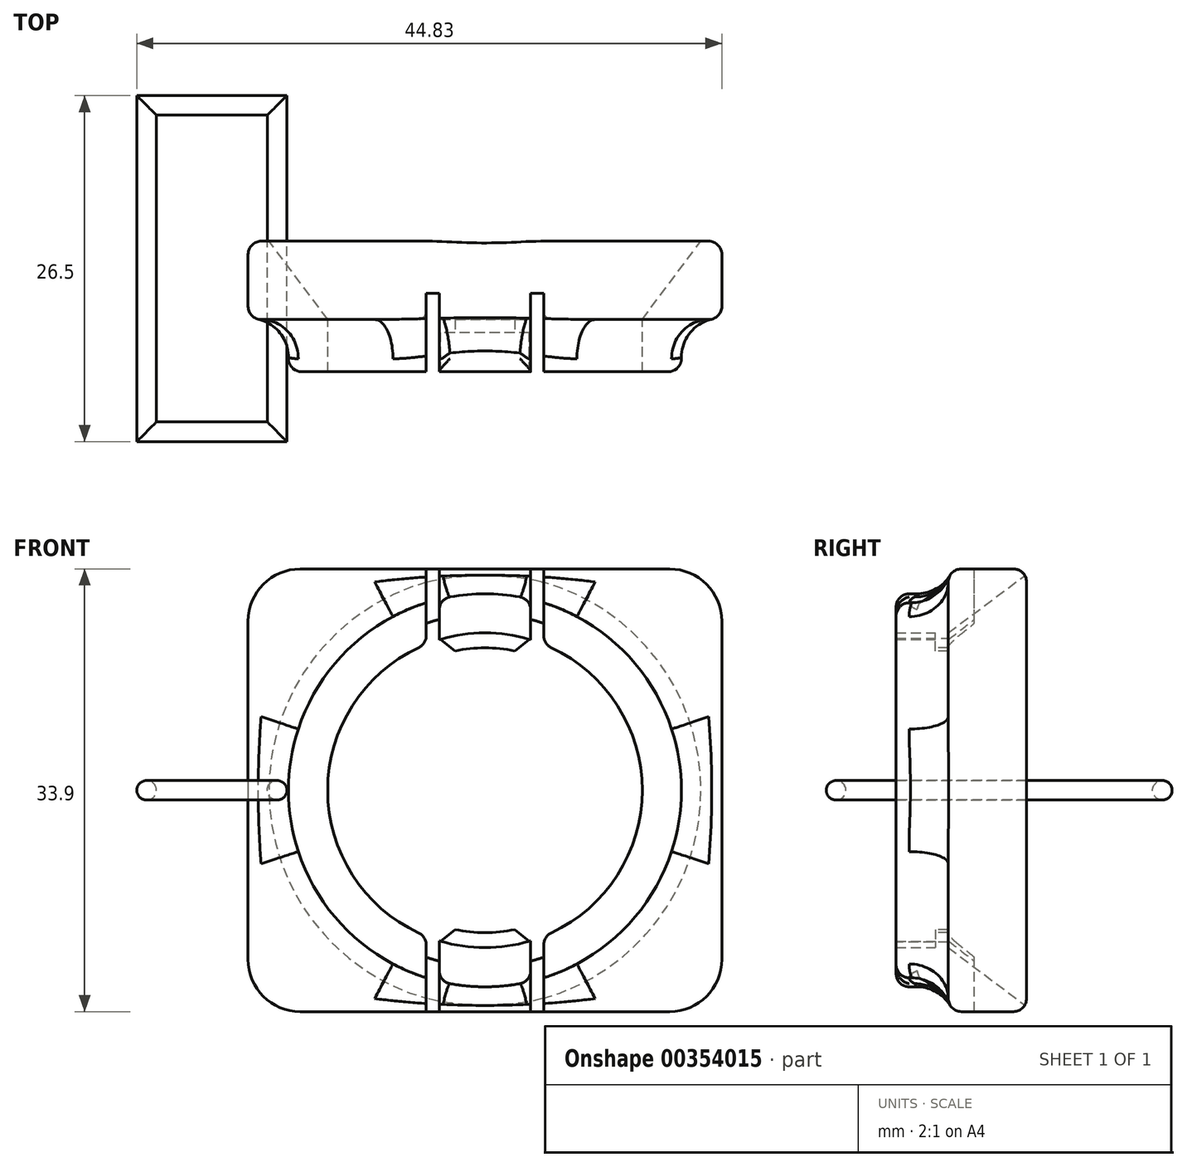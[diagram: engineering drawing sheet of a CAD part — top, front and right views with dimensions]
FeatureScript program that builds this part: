
annotation { "Feature Type Name" : "Feature", "Feature Type Description" : "" }
export const myFeature = defineFeature(function(context is Context, id is Id, definition is map)
    precondition{}
    {
        {
            var Q0;
            Q0=qCreatedBy(makeId("Front.planeOp"),FACE);
            cPlane(context, id + "F0", {"entities" : qUnion([Q0]), "cplaneType" : CPlaneType.OFFSET, "offset" : 3 * mm, "width" : 150 * mm, "height" : 150 * mm});
        }
        {
            var Q0;
            Q0=qCreatedBy(makeId("Front.planeOp"),FACE);
            var sketch = newSketch(context, id + "F1", { "sketchPlane" : qUnion([Q0])});
            skCircle(sketch, "E0", {"center": v(0, 0) * mm, "radius": 12.05 * mm});
            skCircle(sketch, "E1", {"center": v(0, 0) * mm, "radius": 15.05 * mm});
            skSolve(sketch);
        }
        {
            var Q0;
            Q0=makeQuery(id+"F1.imprint","IMPRINT",FACE,{"disambiguationData":[TD([[makeQuery(id+"F1.imprint","IMPRINT",EDGE,{"derivedFrom":sQuery(id+"F1.wireOp",EDGE,"E0")}),-1.0]])]});
            extrude(context, id + "F2", {"entities" : qUnion([Q0]), "offsetDistance" : 25 * mm, "depth" : 7 * mm});
        }
        {
            var Q0;
            Q0=qCreatedBy(id+"F0.planeOp",FACE);
            var sketch = newSketch(context, id + "F3", { "sketchPlane" : qUnion([Q0])});
            skLineSegment(sketch, "E2.bottom", {"start": v(14.15, 16.95) * mm, "end": v(-14.15, 16.95) * mm});
            skLineSegment(sketch, "E2.top", {"start": v(14.15, -16.95) * mm, "end": v(-14.15, -16.95) * mm});
            skLineSegment(sketch, "E2.left", {"start": v(18.15, 12.95) * mm, "end": v(18.15, -12.95) * mm});
            skLineSegment(sketch, "E2.right", {"start": v(-18.15, 12.95) * mm, "end": v(-18.15, -12.95) * mm});
            skPoint(sketch, "E2.middle", {"position": v(0, 0) * mm});
            skPoint(sketch, "E3.visualSharp", {"position": v(-18.15, 16.95) * mm});
            skArc(sketch, "E3.filletArc", {"start": v(-14.15, 16.95) * mm, "mid": v(-16.98, 15.78) * mm, "end": v(-18.15, 12.95) * mm});
            skPoint(sketch, "E4.visualSharp", {"position": v(18.15, 16.95) * mm});
            skArc(sketch, "E4.filletArc", {"start": v(18.15, 12.95) * mm, "mid": v(16.98, 15.78) * mm, "end": v(14.15, 16.95) * mm});
            skPoint(sketch, "E5.visualSharp", {"position": v(18.15, -16.95) * mm});
            skArc(sketch, "E5.filletArc", {"start": v(14.15, -16.95) * mm, "mid": v(16.98, -15.78) * mm, "end": v(18.15, -12.95) * mm});
            skPoint(sketch, "E6.visualSharp", {"position": v(-18.15, -16.95) * mm});
            skArc(sketch, "E6.filletArc", {"start": v(-18.15, -12.95) * mm, "mid": v(-16.98, -15.78) * mm, "end": v(-14.15, -16.95) * mm});
            skCircle(sketch, "E7.0", {"center": v(0, 0) * mm, "radius": 12.05 * mm});
            skSolve(sketch);
        }
        {
            var Q0;
            Q0=makeQuery(id+"F3.imprint","IMPRINT",FACE,{"disambiguationData":[TD([[makeQuery(id+"F3.imprint","IMPRINT",EDGE,{"derivedFrom":sQuery(id+"F3.wireOp",EDGE,"E2.bottom")}),1.0]])]});
            var Q1;
            Q1=makeQuery(id+"F3.imprint","IMPRINT",FACE,{"disambiguationData":[TD([[makeQuery(id+"F3.imprint","IMPRINT",EDGE,{"derivedFrom":makeQuery(id+"FoU0qOtWHECPn0t_1.opExtrude","CAP_EDGE",EDGE,{"disambiguationData":[OSD([sQuery(id+"F1.wireOp",EDGE,"E0")])],"isStart":false})}),1.0]])]});
            extrude(context, id + "F4", {"entities" : qUnion([Q0, Q1]), "operationType" : NewBodyOperationType.ADD, "oppositeDirection" : true, "offsetDistance" : 25 * mm, "depth" : 6 * mm});
        }
        {
            var Q0;
            Q0=makeQuery(id+"F4.opExtrude","CAP_EDGE",EDGE,{"disambiguationData":[OSD([sQuery(id+"F3.wireOp",EDGE,"E7.0")])],"isStart":false});
            chamfer(context, id + "F5", {"entities" : qUnion([Q0]), "chamferType" : ChamferType.TWO_OFFSETS, "width1" : 4.5 * mm, "oppositeDirection" : false, "width2" : 6 * mm, "tangentPropagation" : true});
        }
        {
            var Q0;
            Q0=qCreatedBy(makeId("Right.planeOp"),FACE);
            cPlane(context, id + "F6", {"entities" : qUnion([Q0]), "cplaneType" : CPlaneType.OFFSET, "offset" : 3.5 * mm, "width" : 150 * mm, "height" : 150 * mm});
        }
        {
            var Q0;
            Q0=qCreatedBy(makeId("Top.planeOp"),FACE);
            var sketch = newSketch(context, id + "F7", { "sketchPlane" : qUnion([Q0])});
            skLineSegment(sketch, "E8.0", {"start": v(-14.15, -3) * mm, "end": v(14.15, -3) * mm});
            skLineSegment(sketch, "E9", {"start": v(3.5, -3) * mm, "end": v(3.5, -7) * mm});
            skLineSegment(sketch, "E10", {"start": v(0, 0) * mm, "end": v(0, -13.71) * mm, "construction": true});
            skLineSegment(sketch, "E11", {"start": v(3.5, -7) * mm, "end": v(4.5, -7) * mm});
            skLineSegment(sketch, "E12", {"start": v(4.5, -7) * mm, "end": v(4.5, -3) * mm});
            skLineSegment(sketch, "E13.MirrorCS", {"start": v(-4.5, -7) * mm, "end": v(-4.5, -3) * mm});
            skLineSegment(sketch, "E14.MirrorCS", {"start": v(-3.5, -7) * mm, "end": v(-4.5, -7) * mm});
            skLineSegment(sketch, "E15.MirrorCS", {"start": v(-3.5, -3) * mm, "end": v(-3.5, -7) * mm});
            skLineSegment(sketch, "E16", {"start": v(-4.5, -3) * mm, "end": v(-4.5, -1) * mm});
            skLineSegment(sketch, "E17", {"start": v(-4.5, -1) * mm, "end": v(-3.5, -1) * mm});
            skLineSegment(sketch, "E18", {"start": v(-3.5, -1) * mm, "end": v(-3.5, -3) * mm});
            skLineSegment(sketch, "E19", {"start": v(3.5, -3) * mm, "end": v(3.5, -1) * mm});
            skLineSegment(sketch, "E20", {"start": v(3.5, -1) * mm, "end": v(4.5, -1) * mm});
            skLineSegment(sketch, "E21", {"start": v(4.5, -1) * mm, "end": v(4.5, -3) * mm});
            skSolve(sketch);
        }
        {
            var Q0;
            {var subQ0=sQuery(id+"F7.wireOp",EDGE,"E13.MirrorCS");Q0=makeQuery(id+"F7.imprint","IMPRINT",FACE,{"disambiguationData":[TD([[makeQuery(id+"F7.imprint","IMPRINT",EDGE,{"derivedFrom":subQ0}),-1.0]])]});}
            var Q1;
            {var subQ0=sQuery(id+"F7.wireOp",EDGE,"E9");Q1=makeQuery(id+"F7.imprint","IMPRINT",FACE,{"disambiguationData":[TD([[makeQuery(id+"F7.imprint","IMPRINT",EDGE,{"derivedFrom":subQ0}),1.0]])]});}
            extrude(context, id + "F8", {"entities" : qUnion([Q0, Q1]), "operationType" : NewBodyOperationType.REMOVE, "endBound" : BoundingType.THROUGH_ALL, "oppositeDirection" : true, "offsetDistance" : 25 * mm, "depth" : 25 * mm, "hasSecondDirection" : true, "secondDirectionOppositeDirection" : false, "secondDirectionDepth" : 25 * mm});
        }
        {
            var Q0;
            {var subQ0=sQuery(id+"F1.wireOp",EDGE,"E1");var subQ1=sQuery(id+"F1.wireOp",EDGE,"E0");Q0=makeQuery(id+"F8.boolean.opBoolean","SPLIT",FACE,{"disambiguationData":[TD([makeQuery(id+"F2.opExtrude","SWEPT_FACE",FACE,{"disambiguationData":[OSD([subQ1])]}),makeQuery(id+"F2.opExtrude","SWEPT_FACE",FACE,{"disambiguationData":[OSD([subQ0])]}),makeQuery(id+"FoU0qOtWHECPn0t_1.opExtrude","SWEPT_FACE",FACE,{"disambiguationData":[OSD([subQ1])]}),makeQuery(id+"FoU0qOtWHECPn0t_1.opExtrude","SWEPT_FACE",FACE,{"disambiguationData":[OSD([subQ0])]}),makeQuery(id+"F4.opExtrude","SWEPT_FACE",FACE,{"disambiguationData":[OSD([subQ1])]}),makeQuery(id+"F8.opExtrude","SWEPT_FACE",FACE,{"disambiguationData":[OSD([sQuery(id+"F7.wireOp",EDGE,"E9")])]}),makeQuery(id+"F8.opExtrude","SWEPT_FACE",FACE,{"disambiguationData":[OSD([sQuery(id+"F7.wireOp",EDGE,"E15.MirrorCS")])]})]),OD(1.0)],"derivedFrom":makeQuery(id+"F2.opExtrude","CAP_FACE",FACE,{"disambiguationData":[OSD([subQ1,subQ0])],"isStart":false})});}
            cPlane(context, id + "F9", {"entities" : qUnion([Q0]), "cplaneType" : CPlaneType.OFFSET, "offset" : 3 * mm, "oppositeDirection" : true, "width" : 150 * mm, "height" : 150 * mm});
        }
        {
            var Q0;
            Q0=qCreatedBy(id+"F9.planeOp",FACE);
            var sketch = newSketch(context, id + "F10", { "sketchPlane" : qUnion([Q0])});
            skArc(sketch, "E22.0", {"start": v(3.5, 11.53) * mm, "mid": v(0, 12.05) * mm, "end": v(-3.5, 11.53) * mm});
            skArc(sketch, "E23.0", {"start": v(-3.5, -11.53) * mm, "mid": v(0, -12.05) * mm, "end": v(3.5, -11.53) * mm});
            skLineSegment(sketch, "E24", {"start": v(-3.5, 11.53) * mm, "end": v(-3.5, 10.33) * mm});
            skLineSegment(sketch, "E25", {"start": v(3.5, 10.33) * mm, "end": v(3.5, 11.53) * mm});
            skLineSegment(sketch, "E26", {"start": v(-3.5, -11.53) * mm, "end": v(-3.5, -10.33) * mm});
            skLineSegment(sketch, "E27", {"start": v(3.5, -10.33) * mm, "end": v(3.5, -11.53) * mm});
            skArc(sketch, "E28", {"start": v(3.5, -10.33) * mm, "mid": v(0, -10.9) * mm, "end": v(-3.5, -10.33) * mm});
            skArc(sketch, "E29", {"start": v(3.5, 10.33) * mm, "mid": v(0, 10.9) * mm, "end": v(-3.5, 10.33) * mm});
            skSolve(sketch);
        }
        {
            var Q0;
            Q0=makeQuery(id+"F10.imprint","IMPRINT",FACE,{"disambiguationData":[TD([[makeQuery(id+"F10.imprint","IMPRINT",EDGE,{"derivedFrom":sQuery(id+"F10.wireOp",EDGE,"E23.0")}),1.0]])]});
            var Q1;
            Q1=makeQuery(id+"F10.imprint","IMPRINT",FACE,{"disambiguationData":[TD([[makeQuery(id+"F10.imprint","IMPRINT",EDGE,{"derivedFrom":sQuery(id+"F10.wireOp",EDGE,"E22.0")}),1.0]])]});
            extrude(context, id + "F11", {"entities" : qUnion([Q0, Q1]), "operationType" : NewBodyOperationType.ADD, "oppositeDirection" : true, "depth" : 1 * mm});
        }
        {
            var Q0;
            Q0=makeQuery(id+"F11.opExtrude","SWEPT_EDGE",EDGE,{"disambiguationData":[OSD([sQuery(id+"F10.wireOp",EDGE,"E25"),sQuery(id+"F10.wireOp",EDGE,"E29")])]});
            var Q1;
            Q1=makeQuery(id+"F11.opExtrude","SWEPT_EDGE",EDGE,{"disambiguationData":[OSD([sQuery(id+"F10.wireOp",EDGE,"E24"),sQuery(id+"F10.wireOp",EDGE,"E29")])]});
            var Q2;
            Q2=makeQuery(id+"F11.opExtrude","SWEPT_EDGE",EDGE,{"disambiguationData":[OSD([sQuery(id+"F10.wireOp",EDGE,"E27"),sQuery(id+"F10.wireOp",EDGE,"E28")])]});
            var Q3;
            Q3=makeQuery(id+"F11.opExtrude","SWEPT_EDGE",EDGE,{"disambiguationData":[OSD([sQuery(id+"F10.wireOp",EDGE,"E26"),sQuery(id+"F10.wireOp",EDGE,"E28")])]});
            chamfer(context, id + "F12", {"entities" : qUnion([Q0, Q1, Q2, Q3]), "width" : 1 * mm});
        }
        {
            var Q0;
            {var subQ0=sQuery(id+"F7.wireOp",EDGE,"E16");Q0=makeQuery(id+"F7.imprint","IMPRINT",FACE,{"disambiguationData":[TD([[makeQuery(id+"F7.imprint","IMPRINT",EDGE,{"derivedFrom":subQ0}),-1.0]])]});}
            var Q1;
            {var subQ0=sQuery(id+"F7.wireOp",EDGE,"E19");Q1=makeQuery(id+"F7.imprint","IMPRINT",FACE,{"disambiguationData":[TD([[makeQuery(id+"F7.imprint","IMPRINT",EDGE,{"derivedFrom":subQ0}),-1.0]])]});}
            extrude(context, id + "F13", {"entities" : qUnion([Q0, Q1]), "operationType" : NewBodyOperationType.REMOVE, "endBound" : BoundingType.THROUGH_ALL, "oppositeDirection" : true, "depth" : 25 * mm, "offsetDistance" : 25 * mm, "hasSecondDirection" : true, "secondDirectionBound" : SecondDirectionBoundingType.THROUGH_ALL, "secondDirectionOppositeDirection" : false, "secondDirectionDepth" : 25 * mm});
        }
        {
            var Q0;
            Q0=makeQuery(id+"F4.opExtrude","CAP_EDGE",EDGE,{"disambiguationData":[OSD([sQuery(id+"F3.wireOp",EDGE,"E2.right")])],"isStart":false});
            var Q1;
            Q1=makeQuery(id+"F4.opExtrude","CAP_EDGE",EDGE,{"disambiguationData":[OSD([sQuery(id+"F3.wireOp",EDGE,"E2.right")])],"isStart":true});
            var Q2;
            Q2=makeQuery(id+"F4.opExtrude","CAP_EDGE",EDGE,{"disambiguationData":[OSD([sQuery(id+"F3.wireOp",EDGE,"E2.left")])],"isStart":true});
            var Q3;
            {var subQ0=sQuery(id+"F7.wireOp",EDGE,"E19");var subQ1=sQuery(id+"F7.wireOp",EDGE,"E9");var subQ2=sQuery(id+"F7.wireOp",EDGE,"E8.0");var subQ3=makeQuery(id+"F8.opExtrude","SWEPT_FACE",FACE,{"disambiguationData":[OSD([subQ2]),TDD([makeQuery(id+"F7.imprint","IMPRINT",EDGE,{"disambiguationData":[TD([[makeQuery(id+"F7.imprint","INTERSECT",VERTEX,{"derivedFrom":[subQ2,subQ1,subQ0]}),-1.0]])],"derivedFrom":subQ2})])]});var subQ4=sQuery(id+"F3.wireOp",EDGE,"E2.top");var subQ5=makeQuery(id+"F4.opExtrude","SWEPT_FACE",FACE,{"disambiguationData":[OSD([subQ4])]});var subQ8=makeQuery(id+"F8.opExtrude","SWEPT_FACE",FACE,{"disambiguationData":[OSD([subQ2]),TDD([makeQuery(id+"F7.imprint","IMPRINT",EDGE,{"disambiguationData":[TD([[makeQuery(id+"F7.imprint","INTERSECT",VERTEX,{"derivedFrom":[subQ2,sQuery(id+"F7.wireOp",EDGE,"E13.MirrorCS"),sQuery(id+"F7.wireOp",EDGE,"E16")]}),-1.0]])],"derivedFrom":subQ2})])]});Q3=makeQuery(id+"F13.boolean.opBoolean","SPLIT",EDGE,{"disambiguationData":[TD([makeQuery(id+"F8.boolean.opBoolean","COPY",FACE,{"disambiguationData":[OD(0.0)],"derivedFrom":makeQuery(id+"F8.opExtrude","SWEPT_FACE",FACE,{"disambiguationData":[OSD([subQ1])]})})])],"derivedFrom":makeQuery(id+"F8.boolean.opBoolean","INTERSECT",EDGE,{"disambiguationData":[topologyDisambiguationEdgeConnected([subQ5])],"derivedFrom":[subQ8,subQ3]})});}
            var Q4;
            {var subQ0=sQuery(id+"F7.wireOp",EDGE,"E19");var subQ1=sQuery(id+"F7.wireOp",EDGE,"E9");var subQ2=sQuery(id+"F7.wireOp",EDGE,"E8.0");var subQ3=makeQuery(id+"F8.opExtrude","SWEPT_FACE",FACE,{"disambiguationData":[OSD([subQ2]),TDD([makeQuery(id+"F7.imprint","IMPRINT",EDGE,{"disambiguationData":[TD([[makeQuery(id+"F7.imprint","INTERSECT",VERTEX,{"derivedFrom":[subQ2,subQ1,subQ0]}),-1.0]])],"derivedFrom":subQ2})])]});var subQ6=makeQuery(id+"F8.opExtrude","SWEPT_FACE",FACE,{"disambiguationData":[OSD([subQ2]),TDD([makeQuery(id+"F7.imprint","IMPRINT",EDGE,{"disambiguationData":[TD([[makeQuery(id+"F7.imprint","INTERSECT",VERTEX,{"derivedFrom":[subQ2,sQuery(id+"F7.wireOp",EDGE,"E13.MirrorCS"),sQuery(id+"F7.wireOp",EDGE,"E16")]}),-1.0]])],"derivedFrom":subQ2})])]});var subQ7=sQuery(id+"F3.wireOp",EDGE,"E2.bottom");var subQ9=makeQuery(id+"F4.opExtrude","SWEPT_FACE",FACE,{"disambiguationData":[OSD([subQ7])]});Q4=makeQuery(id+"F13.boolean.opBoolean","SPLIT",EDGE,{"disambiguationData":[TD([makeQuery(id+"F8.boolean.opBoolean","COPY",FACE,{"disambiguationData":[OD(1.0)],"derivedFrom":makeQuery(id+"F8.opExtrude","SWEPT_FACE",FACE,{"disambiguationData":[OSD([subQ1])]})})])],"derivedFrom":makeQuery(id+"F8.boolean.opBoolean","INTERSECT",EDGE,{"disambiguationData":[topologyDisambiguationEdgeConnected([subQ9])],"derivedFrom":[subQ6,subQ3]})});}
            fillet(context, id + "F14", {"entities" : qUnion([Q0, Q1, Q2, Q3, Q4]), "radius" : 1 * mm, "tangentPropagation" : true, "allowEdgeOverflow" : false});
        }
        {
            var Q0;
            {var subQ0=sQuery(id+"F7.wireOp",EDGE,"E12");var subQ1=makeQuery(id+"F8.opExtrude","SWEPT_FACE",FACE,{"disambiguationData":[OSD([subQ0])]});var subQ2=sQuery(id+"F7.wireOp",EDGE,"E8.0");var subQ3=sQuery(id+"F1.wireOp",EDGE,"E1");Q0=makeQuery(id+"FviWnsTTXuQefTK_1.opFillet","BLEND_EDGE",EDGE,{"blendedFrom":[makeQuery(id+"F8.boolean.opBoolean","SPLIT",EDGE,{"disambiguationData":[TD([makeQuery(id+"F2.opExtrude","SWEPT_FACE",FACE,{"disambiguationData":[OSD([subQ3])]}),makeQuery(id+"FoU0qOtWHECPn0t_1.opExtrude","SWEPT_FACE",FACE,{"disambiguationData":[OSD([subQ3])]}),makeQuery(id+"F4.opExtrude","CAP_FACE",FACE,{"disambiguationData":[OSD([sQuery(id+"F1.wireOp",EDGE,"E0"),sQuery(id+"F3.wireOp",EDGE,"E2.bottom"),sQuery(id+"F3.wireOp",EDGE,"E2.top"),sQuery(id+"F3.wireOp",EDGE,"E2.left"),sQuery(id+"F3.wireOp",EDGE,"E2.right"),sQuery(id+"F3.wireOp",EDGE,"E3.filletArc"),sQuery(id+"F3.wireOp",EDGE,"E4.filletArc"),sQuery(id+"F3.wireOp",EDGE,"E5.filletArc"),sQuery(id+"F3.wireOp",EDGE,"E6.filletArc")])],"isStart":true}),makeQuery(id+"F8.opExtrude","SWEPT_FACE",FACE,{"disambiguationData":[OSD([subQ2]),TDD([makeQuery(id+"F7.imprint","IMPRINT",EDGE,{"disambiguationData":[TD([[makeQuery(id+"F7.imprint","INTERSECT",VERTEX,{"derivedFrom":[subQ2,sQuery(id+"F7.wireOp",EDGE,"E13.MirrorCS")]}),-1.0]])],"derivedFrom":subQ2})])]}),makeQuery(id+"F8.opExtrude","SWEPT_FACE",FACE,{"disambiguationData":[OSD([subQ2]),TDD([makeQuery(id+"F7.imprint","IMPRINT",EDGE,{"disambiguationData":[TD([[makeQuery(id+"F7.imprint","INTERSECT",VERTEX,{"derivedFrom":[subQ2,sQuery(id+"F7.wireOp",EDGE,"E9")]}),-1.0]])],"derivedFrom":subQ2})])]}),subQ1])],"derivedFrom":makeQuery(id+"FoU0qOtWHECPn0t_1.opExtrude","CAP_EDGE",EDGE,{"disambiguationData":[OSD([subQ3])],"isStart":false})}),makeQuery(id+"F8.boolean.opBoolean","COPY",FACE,{"disambiguationData":[OD(0.0)],"derivedFrom":subQ1})],"blendedInto":[makeQuery(id+"F8.boolean.opBoolean","COPY",FACE,{"disambiguationData":[OD(0.0)],"derivedFrom":subQ1})]});}
            var Q1;
            {var subQ0=sQuery(id+"F7.wireOp",EDGE,"E13.MirrorCS");var subQ1=makeQuery(id+"F8.opExtrude","SWEPT_FACE",FACE,{"disambiguationData":[OSD([subQ0])]});var subQ2=sQuery(id+"F7.wireOp",EDGE,"E8.0");var subQ3=sQuery(id+"F1.wireOp",EDGE,"E1");Q1=makeQuery(id+"FviWnsTTXuQefTK_1.opFillet","BLEND_EDGE",EDGE,{"blendedFrom":[makeQuery(id+"F8.boolean.opBoolean","SPLIT",EDGE,{"disambiguationData":[TD([makeQuery(id+"F2.opExtrude","SWEPT_FACE",FACE,{"disambiguationData":[OSD([subQ3])]}),makeQuery(id+"FoU0qOtWHECPn0t_1.opExtrude","SWEPT_FACE",FACE,{"disambiguationData":[OSD([subQ3])]}),makeQuery(id+"F4.opExtrude","CAP_FACE",FACE,{"disambiguationData":[OSD([sQuery(id+"F1.wireOp",EDGE,"E0"),sQuery(id+"F3.wireOp",EDGE,"E2.bottom"),sQuery(id+"F3.wireOp",EDGE,"E2.top"),sQuery(id+"F3.wireOp",EDGE,"E2.left"),sQuery(id+"F3.wireOp",EDGE,"E2.right"),sQuery(id+"F3.wireOp",EDGE,"E3.filletArc"),sQuery(id+"F3.wireOp",EDGE,"E4.filletArc"),sQuery(id+"F3.wireOp",EDGE,"E5.filletArc"),sQuery(id+"F3.wireOp",EDGE,"E6.filletArc")])],"isStart":true}),makeQuery(id+"F8.opExtrude","SWEPT_FACE",FACE,{"disambiguationData":[OSD([subQ2]),TDD([makeQuery(id+"F7.imprint","IMPRINT",EDGE,{"disambiguationData":[TD([[makeQuery(id+"F7.imprint","INTERSECT",VERTEX,{"derivedFrom":[subQ2,subQ0]}),-1.0]])],"derivedFrom":subQ2})])]}),makeQuery(id+"F8.opExtrude","SWEPT_FACE",FACE,{"disambiguationData":[OSD([subQ2]),TDD([makeQuery(id+"F7.imprint","IMPRINT",EDGE,{"disambiguationData":[TD([[makeQuery(id+"F7.imprint","INTERSECT",VERTEX,{"derivedFrom":[subQ2,sQuery(id+"F7.wireOp",EDGE,"E9")]}),-1.0]])],"derivedFrom":subQ2})])]}),subQ1])],"derivedFrom":makeQuery(id+"FoU0qOtWHECPn0t_1.opExtrude","CAP_EDGE",EDGE,{"disambiguationData":[OSD([subQ3])],"isStart":false})}),makeQuery(id+"F8.boolean.opBoolean","COPY",FACE,{"disambiguationData":[OD(0.0)],"derivedFrom":subQ1})],"blendedInto":[makeQuery(id+"F8.boolean.opBoolean","COPY",FACE,{"disambiguationData":[OD(0.0)],"derivedFrom":subQ1})]});}
            var Q2;
            {var subQ0=sQuery(id+"F1.wireOp",EDGE,"E1");Q2=makeQuery(id+"F8.boolean.opBoolean","INTERSECT",EDGE,{"disambiguationData":[OD(0.0)],"derivedFrom":[makeQuery(id+"FoU0qOtWHECPn0t_1.boolean.opBoolean","MERGE",FACE,{"derivedFrom":[makeQuery(id+"F2.opExtrude","SWEPT_FACE",FACE,{"disambiguationData":[OSD([subQ0])]}),makeQuery(id+"FoU0qOtWHECPn0t_1.opExtrude","SWEPT_FACE",FACE,{"disambiguationData":[OSD([subQ0])]})]}),makeQuery(id+"F8.opExtrude","SWEPT_FACE",FACE,{"disambiguationData":[OSD([sQuery(id+"F7.wireOp",EDGE,"E15.MirrorCS")])]})]});}
            var Q3;
            {var subQ0=sQuery(id+"F1.wireOp",EDGE,"E1");Q3=makeQuery(id+"F8.boolean.opBoolean","INTERSECT",EDGE,{"disambiguationData":[OD(0.0)],"derivedFrom":[makeQuery(id+"FoU0qOtWHECPn0t_1.boolean.opBoolean","MERGE",FACE,{"derivedFrom":[makeQuery(id+"F2.opExtrude","SWEPT_FACE",FACE,{"disambiguationData":[OSD([subQ0])]}),makeQuery(id+"FoU0qOtWHECPn0t_1.opExtrude","SWEPT_FACE",FACE,{"disambiguationData":[OSD([subQ0])]})]}),makeQuery(id+"F8.opExtrude","SWEPT_FACE",FACE,{"disambiguationData":[OSD([sQuery(id+"F7.wireOp",EDGE,"E9")])]})]});}
            var Q4;
            {var subQ0=sQuery(id+"F7.wireOp",EDGE,"E12");var subQ1=makeQuery(id+"F8.opExtrude","SWEPT_FACE",FACE,{"disambiguationData":[OSD([subQ0])]});var subQ2=sQuery(id+"F7.wireOp",EDGE,"E8.0");var subQ3=sQuery(id+"F1.wireOp",EDGE,"E1");Q4=makeQuery(id+"FviWnsTTXuQefTK_1.opFillet","BLEND_EDGE",EDGE,{"blendedFrom":[makeQuery(id+"F8.boolean.opBoolean","SPLIT",EDGE,{"disambiguationData":[TD([makeQuery(id+"F2.opExtrude","SWEPT_FACE",FACE,{"disambiguationData":[OSD([subQ3])]}),makeQuery(id+"FoU0qOtWHECPn0t_1.opExtrude","SWEPT_FACE",FACE,{"disambiguationData":[OSD([subQ3])]}),makeQuery(id+"F4.opExtrude","CAP_FACE",FACE,{"disambiguationData":[OSD([sQuery(id+"F1.wireOp",EDGE,"E0"),sQuery(id+"F3.wireOp",EDGE,"E2.bottom"),sQuery(id+"F3.wireOp",EDGE,"E2.top"),sQuery(id+"F3.wireOp",EDGE,"E2.left"),sQuery(id+"F3.wireOp",EDGE,"E2.right"),sQuery(id+"F3.wireOp",EDGE,"E3.filletArc"),sQuery(id+"F3.wireOp",EDGE,"E4.filletArc"),sQuery(id+"F3.wireOp",EDGE,"E5.filletArc"),sQuery(id+"F3.wireOp",EDGE,"E6.filletArc")])],"isStart":true}),makeQuery(id+"F8.opExtrude","SWEPT_FACE",FACE,{"disambiguationData":[OSD([subQ2]),TDD([makeQuery(id+"F7.imprint","IMPRINT",EDGE,{"disambiguationData":[TD([[makeQuery(id+"F7.imprint","INTERSECT",VERTEX,{"derivedFrom":[subQ2,sQuery(id+"F7.wireOp",EDGE,"E13.MirrorCS")]}),-1.0]])],"derivedFrom":subQ2})])]}),makeQuery(id+"F8.opExtrude","SWEPT_FACE",FACE,{"disambiguationData":[OSD([subQ2]),TDD([makeQuery(id+"F7.imprint","IMPRINT",EDGE,{"disambiguationData":[TD([[makeQuery(id+"F7.imprint","INTERSECT",VERTEX,{"derivedFrom":[subQ2,sQuery(id+"F7.wireOp",EDGE,"E9")]}),-1.0]])],"derivedFrom":subQ2})])]}),subQ1])],"derivedFrom":makeQuery(id+"FoU0qOtWHECPn0t_1.opExtrude","CAP_EDGE",EDGE,{"disambiguationData":[OSD([subQ3])],"isStart":false})}),makeQuery(id+"F8.boolean.opBoolean","COPY",FACE,{"disambiguationData":[OD(1.0)],"derivedFrom":subQ1})],"blendedInto":[makeQuery(id+"F8.boolean.opBoolean","COPY",FACE,{"disambiguationData":[OD(1.0)],"derivedFrom":subQ1})]});}
            var Q5;
            {var subQ0=sQuery(id+"F7.wireOp",EDGE,"E13.MirrorCS");var subQ1=makeQuery(id+"F8.opExtrude","SWEPT_FACE",FACE,{"disambiguationData":[OSD([subQ0])]});var subQ2=sQuery(id+"F7.wireOp",EDGE,"E8.0");var subQ3=sQuery(id+"F1.wireOp",EDGE,"E1");Q5=makeQuery(id+"FviWnsTTXuQefTK_1.opFillet","BLEND_EDGE",EDGE,{"blendedFrom":[makeQuery(id+"F8.boolean.opBoolean","SPLIT",EDGE,{"disambiguationData":[TD([makeQuery(id+"F2.opExtrude","SWEPT_FACE",FACE,{"disambiguationData":[OSD([subQ3])]}),makeQuery(id+"FoU0qOtWHECPn0t_1.opExtrude","SWEPT_FACE",FACE,{"disambiguationData":[OSD([subQ3])]}),makeQuery(id+"F4.opExtrude","CAP_FACE",FACE,{"disambiguationData":[OSD([sQuery(id+"F1.wireOp",EDGE,"E0"),sQuery(id+"F3.wireOp",EDGE,"E2.bottom"),sQuery(id+"F3.wireOp",EDGE,"E2.top"),sQuery(id+"F3.wireOp",EDGE,"E2.left"),sQuery(id+"F3.wireOp",EDGE,"E2.right"),sQuery(id+"F3.wireOp",EDGE,"E3.filletArc"),sQuery(id+"F3.wireOp",EDGE,"E4.filletArc"),sQuery(id+"F3.wireOp",EDGE,"E5.filletArc"),sQuery(id+"F3.wireOp",EDGE,"E6.filletArc")])],"isStart":true}),makeQuery(id+"F8.opExtrude","SWEPT_FACE",FACE,{"disambiguationData":[OSD([subQ2]),TDD([makeQuery(id+"F7.imprint","IMPRINT",EDGE,{"disambiguationData":[TD([[makeQuery(id+"F7.imprint","INTERSECT",VERTEX,{"derivedFrom":[subQ2,subQ0]}),-1.0]])],"derivedFrom":subQ2})])]}),makeQuery(id+"F8.opExtrude","SWEPT_FACE",FACE,{"disambiguationData":[OSD([subQ2]),TDD([makeQuery(id+"F7.imprint","IMPRINT",EDGE,{"disambiguationData":[TD([[makeQuery(id+"F7.imprint","INTERSECT",VERTEX,{"derivedFrom":[subQ2,sQuery(id+"F7.wireOp",EDGE,"E9")]}),-1.0]])],"derivedFrom":subQ2})])]}),subQ1])],"derivedFrom":makeQuery(id+"FoU0qOtWHECPn0t_1.opExtrude","CAP_EDGE",EDGE,{"disambiguationData":[OSD([subQ3])],"isStart":false})}),makeQuery(id+"F8.boolean.opBoolean","COPY",FACE,{"disambiguationData":[OD(1.0)],"derivedFrom":subQ1})],"blendedInto":[makeQuery(id+"F8.boolean.opBoolean","COPY",FACE,{"disambiguationData":[OD(1.0)],"derivedFrom":subQ1})]});}
            var Q6;
            {var subQ0=sQuery(id+"F1.wireOp",EDGE,"E1");Q6=makeQuery(id+"F8.boolean.opBoolean","INTERSECT",EDGE,{"disambiguationData":[OD(1.0)],"derivedFrom":[makeQuery(id+"FoU0qOtWHECPn0t_1.boolean.opBoolean","MERGE",FACE,{"derivedFrom":[makeQuery(id+"F2.opExtrude","SWEPT_FACE",FACE,{"disambiguationData":[OSD([subQ0])]}),makeQuery(id+"FoU0qOtWHECPn0t_1.opExtrude","SWEPT_FACE",FACE,{"disambiguationData":[OSD([subQ0])]})]}),makeQuery(id+"F8.opExtrude","SWEPT_FACE",FACE,{"disambiguationData":[OSD([sQuery(id+"F7.wireOp",EDGE,"E15.MirrorCS")])]})]});}
            var Q7;
            {var subQ0=sQuery(id+"F1.wireOp",EDGE,"E1");Q7=makeQuery(id+"F8.boolean.opBoolean","INTERSECT",EDGE,{"disambiguationData":[OD(1.0)],"derivedFrom":[makeQuery(id+"FoU0qOtWHECPn0t_1.boolean.opBoolean","MERGE",FACE,{"derivedFrom":[makeQuery(id+"F2.opExtrude","SWEPT_FACE",FACE,{"disambiguationData":[OSD([subQ0])]}),makeQuery(id+"FoU0qOtWHECPn0t_1.opExtrude","SWEPT_FACE",FACE,{"disambiguationData":[OSD([subQ0])]})]}),makeQuery(id+"F8.opExtrude","SWEPT_FACE",FACE,{"disambiguationData":[OSD([sQuery(id+"F7.wireOp",EDGE,"E9")])]})]});}
            var Q8;
            {var subQ0=sQuery(id+"F1.wireOp",EDGE,"E0");Q8=makeQuery(id+"F8.boolean.opBoolean","INTERSECT",EDGE,{"disambiguationData":[OD(0.0)],"derivedFrom":[makeQuery(id+"F4.boolean.opBoolean","MERGE",FACE,{"derivedFrom":[makeQuery(id+"FoU0qOtWHECPn0t_1.boolean.opBoolean","MERGE",FACE,{"derivedFrom":[makeQuery(id+"F2.opExtrude","SWEPT_FACE",FACE,{"disambiguationData":[OSD([subQ0])]}),makeQuery(id+"FoU0qOtWHECPn0t_1.opExtrude","SWEPT_FACE",FACE,{"disambiguationData":[OSD([subQ0])]})]}),makeQuery(id+"F4.opExtrude","SWEPT_FACE",FACE,{"disambiguationData":[OSD([subQ0])]})]}),makeQuery(id+"F8.opExtrude","SWEPT_FACE",FACE,{"disambiguationData":[OSD([sQuery(id+"F7.wireOp",EDGE,"E12")])]})]});}
            var Q9;
            {var subQ0=sQuery(id+"F1.wireOp",EDGE,"E0");Q9=makeQuery(id+"F8.boolean.opBoolean","INTERSECT",EDGE,{"disambiguationData":[OD(0.0)],"derivedFrom":[makeQuery(id+"F4.boolean.opBoolean","MERGE",FACE,{"derivedFrom":[makeQuery(id+"FoU0qOtWHECPn0t_1.boolean.opBoolean","MERGE",FACE,{"derivedFrom":[makeQuery(id+"F2.opExtrude","SWEPT_FACE",FACE,{"disambiguationData":[OSD([subQ0])]}),makeQuery(id+"FoU0qOtWHECPn0t_1.opExtrude","SWEPT_FACE",FACE,{"disambiguationData":[OSD([subQ0])]})]}),makeQuery(id+"F4.opExtrude","SWEPT_FACE",FACE,{"disambiguationData":[OSD([subQ0])]})]}),makeQuery(id+"F8.opExtrude","SWEPT_FACE",FACE,{"disambiguationData":[OSD([sQuery(id+"F7.wireOp",EDGE,"E13.MirrorCS")])]})]});}
            var Q10;
            {var subQ0=sQuery(id+"F1.wireOp",EDGE,"E0");Q10=makeQuery(id+"F8.boolean.opBoolean","INTERSECT",EDGE,{"disambiguationData":[OD(1.0)],"derivedFrom":[makeQuery(id+"F4.boolean.opBoolean","MERGE",FACE,{"derivedFrom":[makeQuery(id+"FoU0qOtWHECPn0t_1.boolean.opBoolean","MERGE",FACE,{"derivedFrom":[makeQuery(id+"F2.opExtrude","SWEPT_FACE",FACE,{"disambiguationData":[OSD([subQ0])]}),makeQuery(id+"FoU0qOtWHECPn0t_1.opExtrude","SWEPT_FACE",FACE,{"disambiguationData":[OSD([subQ0])]})]}),makeQuery(id+"F4.opExtrude","SWEPT_FACE",FACE,{"disambiguationData":[OSD([subQ0])]})]}),makeQuery(id+"F8.opExtrude","SWEPT_FACE",FACE,{"disambiguationData":[OSD([sQuery(id+"F7.wireOp",EDGE,"E12")])]})]});}
            var Q11;
            {var subQ0=sQuery(id+"F1.wireOp",EDGE,"E0");Q11=makeQuery(id+"F8.boolean.opBoolean","INTERSECT",EDGE,{"disambiguationData":[OD(1.0)],"derivedFrom":[makeQuery(id+"F4.boolean.opBoolean","MERGE",FACE,{"derivedFrom":[makeQuery(id+"FoU0qOtWHECPn0t_1.boolean.opBoolean","MERGE",FACE,{"derivedFrom":[makeQuery(id+"F2.opExtrude","SWEPT_FACE",FACE,{"disambiguationData":[OSD([subQ0])]}),makeQuery(id+"FoU0qOtWHECPn0t_1.opExtrude","SWEPT_FACE",FACE,{"disambiguationData":[OSD([subQ0])]})]}),makeQuery(id+"F4.opExtrude","SWEPT_FACE",FACE,{"disambiguationData":[OSD([subQ0])]})]}),makeQuery(id+"F8.opExtrude","SWEPT_FACE",FACE,{"disambiguationData":[OSD([sQuery(id+"F7.wireOp",EDGE,"E13.MirrorCS")])]})]});}
            var Q12;
            {var subQ0=sQuery(id+"F1.wireOp",EDGE,"E1");Q12=makeQuery(id+"F8.boolean.opBoolean","SPLIT",EDGE,{"disambiguationData":[TD([makeQuery(id+"F2.opExtrude","CAP_FACE",FACE,{"disambiguationData":[OSD([sQuery(id+"F1.wireOp",EDGE,"E0"),subQ0])],"isStart":false}),makeQuery(id+"F2.opExtrude","SWEPT_FACE",FACE,{"disambiguationData":[OSD([subQ0])]}),makeQuery(id+"FoU0qOtWHECPn0t_1.opExtrude","SWEPT_FACE",FACE,{"disambiguationData":[OSD([subQ0])]}),makeQuery(id+"F8.opExtrude","SWEPT_FACE",FACE,{"disambiguationData":[OSD([sQuery(id+"F7.wireOp",EDGE,"E13.MirrorCS")])]})])],"derivedFrom":makeQuery(id+"F2.opExtrude","CAP_EDGE",EDGE,{"disambiguationData":[OSD([subQ0])],"isStart":false})});}
            var Q13;
            {var subQ0=sQuery(id+"F1.wireOp",EDGE,"E1");Q13=makeQuery(id+"F8.boolean.opBoolean","SPLIT",EDGE,{"disambiguationData":[TD([makeQuery(id+"F2.opExtrude","CAP_FACE",FACE,{"disambiguationData":[OSD([sQuery(id+"F1.wireOp",EDGE,"E0"),subQ0])],"isStart":false}),makeQuery(id+"F2.opExtrude","SWEPT_FACE",FACE,{"disambiguationData":[OSD([subQ0])]}),makeQuery(id+"FoU0qOtWHECPn0t_1.opExtrude","SWEPT_FACE",FACE,{"disambiguationData":[OSD([subQ0])]}),makeQuery(id+"F8.opExtrude","SWEPT_FACE",FACE,{"disambiguationData":[OSD([sQuery(id+"F7.wireOp",EDGE,"E12")])]})])],"derivedFrom":makeQuery(id+"F2.opExtrude","CAP_EDGE",EDGE,{"disambiguationData":[OSD([subQ0])],"isStart":false})});}
            var Q14;
            {var subQ0=sQuery(id+"F1.wireOp",EDGE,"E1");Q14=makeQuery(id+"F8.boolean.opBoolean","SPLIT",EDGE,{"disambiguationData":[TD([makeQuery(id+"F2.opExtrude","CAP_FACE",FACE,{"disambiguationData":[OSD([sQuery(id+"F1.wireOp",EDGE,"E0"),subQ0])],"isStart":false}),makeQuery(id+"F2.opExtrude","SWEPT_FACE",FACE,{"disambiguationData":[OSD([subQ0])]}),makeQuery(id+"FoU0qOtWHECPn0t_1.opExtrude","SWEPT_FACE",FACE,{"disambiguationData":[OSD([subQ0])]}),makeQuery(id+"F8.opExtrude","SWEPT_FACE",FACE,{"disambiguationData":[OSD([sQuery(id+"F7.wireOp",EDGE,"E9")])]}),makeQuery(id+"F8.opExtrude","SWEPT_FACE",FACE,{"disambiguationData":[OSD([sQuery(id+"F7.wireOp",EDGE,"E15.MirrorCS")])]})]),OD(0.0)],"derivedFrom":makeQuery(id+"F2.opExtrude","CAP_EDGE",EDGE,{"disambiguationData":[OSD([subQ0])],"isStart":false})});}
            var Q15;
            {var subQ0=sQuery(id+"F1.wireOp",EDGE,"E1");Q15=makeQuery(id+"F8.boolean.opBoolean","SPLIT",EDGE,{"disambiguationData":[TD([makeQuery(id+"F2.opExtrude","CAP_FACE",FACE,{"disambiguationData":[OSD([sQuery(id+"F1.wireOp",EDGE,"E0"),subQ0])],"isStart":false}),makeQuery(id+"F2.opExtrude","SWEPT_FACE",FACE,{"disambiguationData":[OSD([subQ0])]}),makeQuery(id+"FoU0qOtWHECPn0t_1.opExtrude","SWEPT_FACE",FACE,{"disambiguationData":[OSD([subQ0])]}),makeQuery(id+"F8.opExtrude","SWEPT_FACE",FACE,{"disambiguationData":[OSD([sQuery(id+"F7.wireOp",EDGE,"E9")])]}),makeQuery(id+"F8.opExtrude","SWEPT_FACE",FACE,{"disambiguationData":[OSD([sQuery(id+"F7.wireOp",EDGE,"E15.MirrorCS")])]})]),OD(1.0)],"derivedFrom":makeQuery(id+"F2.opExtrude","CAP_EDGE",EDGE,{"disambiguationData":[OSD([subQ0])],"isStart":false})});}
            fillet(context, id + "F15", {"entities" : qUnion([Q0, Q1, Q2, Q3, Q4, Q5, Q6, Q7, Q8, Q9, Q10, Q11, Q12, Q13, Q14, Q15]), "radius" : 1 * mm, "tangentPropagation" : true, "allowEdgeOverflow" : false});
        }
        {
            var Q0;
            Q0=qCreatedBy(makeId("Top.planeOp"),FACE);
            var sketch = newSketch(context, id + "F16", { "sketchPlane" : qUnion([Q0])});
            skPoint(sketch, "E30.middle", {"position": v(-20.93, 0.9) * mm});
            skLineSegment(sketch, "E31.bottom", {"start": v(-15.93, 13.4) * mm, "end": v(-25.93, 13.4) * mm});
            skLineSegment(sketch, "E31.top", {"start": v(-15.93, -11.6) * mm, "end": v(-25.93, -11.6) * mm});
            skLineSegment(sketch, "E31.left", {"start": v(-15.93, 13.4) * mm, "end": v(-15.93, -11.6) * mm});
            skLineSegment(sketch, "E31.right", {"start": v(-25.93, 13.4) * mm, "end": v(-25.93, -11.6) * mm});
            skSolve(sketch);
        }
        {
            var Q0;
            Q0=qCreatedBy(makeId("Front.planeOp"),FACE);
            var sketch = newSketch(context, id + "F17", { "sketchPlane" : qUnion([Q0])});
            skCircle(sketch, "E32", {"center": v(-25.93, 0) * mm, "radius": 0.75 * mm});
            skSolve(sketch);
        }
        {
            var Q0;
            Q0=makeQuery(id+"F17.imprint","IMPRINT",FACE,{"disambiguationData":[TD([[makeQuery(id+"F17.imprint","IMPRINT",EDGE,{"derivedFrom":sQuery(id+"F17.wireOp",EDGE,"E32")}),1.0]])]});
            var Q1;
            Q1=sQuery(id+"F16.wireOp",EDGE,"E31.right");
            var Q2;
            Q2=sQuery(id+"F16.wireOp",EDGE,"E31.bottom");
            var Q3;
            Q3=sQuery(id+"F16.wireOp",EDGE,"E31.left");
            var Q4;
            Q4=sQuery(id+"F16.wireOp",EDGE,"E31.top");
            sweep(context, id + "F18", {"profiles" : qUnion([Q0]), "path" : qUnion([Q1, Q2, Q3, Q4])});
        }
        {
            var Q0;
            {var subQ0=sQuery(id+"F7.wireOp",EDGE,"E8.0");var subQ1=sQuery(id+"F7.wireOp",EDGE,"E13.MirrorCS");var subQ2=makeQuery(id+"F2.opExtrude","SWEPT_FACE",FACE,{"disambiguationData":[OSD([sQuery(id+"F1.wireOp",EDGE,"E1")])]});var subQ3=makeQuery(id+"F4.opExtrude","CAP_FACE",FACE,{"disambiguationData":[OSD([sQuery(id+"F3.wireOp",EDGE,"E2.bottom"),sQuery(id+"F3.wireOp",EDGE,"E2.top"),sQuery(id+"F3.wireOp",EDGE,"E2.left"),sQuery(id+"F3.wireOp",EDGE,"E2.right"),sQuery(id+"F3.wireOp",EDGE,"E3.filletArc"),sQuery(id+"F3.wireOp",EDGE,"E4.filletArc"),sQuery(id+"F3.wireOp",EDGE,"E5.filletArc"),sQuery(id+"F3.wireOp",EDGE,"E6.filletArc"),sQuery(id+"F3.wireOp",EDGE,"E7.0")])],"isStart":true});Q0=makeQuery(id+"F8.boolean.opBoolean","SPLIT",EDGE,{"disambiguationData":[TD([subQ2,subQ3,makeQuery(id+"F8.opExtrude","SWEPT_FACE",FACE,{"disambiguationData":[OSD([subQ0]),TDD([makeQuery(id+"F7.imprint","IMPRINT",EDGE,{"disambiguationData":[TD([[makeQuery(id+"F7.imprint","INTERSECT",VERTEX,{"derivedFrom":[subQ0,subQ1,sQuery(id+"F7.wireOp",EDGE,"E16")]}),-1.0]])],"derivedFrom":subQ0})])]}),makeQuery(id+"F8.opExtrude","SWEPT_FACE",FACE,{"disambiguationData":[OSD([subQ0]),TDD([makeQuery(id+"F7.imprint","IMPRINT",EDGE,{"disambiguationData":[TD([[makeQuery(id+"F7.imprint","INTERSECT",VERTEX,{"derivedFrom":[subQ0,sQuery(id+"F7.wireOp",EDGE,"E9"),sQuery(id+"F7.wireOp",EDGE,"E19")]}),-1.0]])],"derivedFrom":subQ0})])]}),makeQuery(id+"F8.opExtrude","SWEPT_FACE",FACE,{"disambiguationData":[OSD([subQ1])]})])],"derivedFrom":makeQuery(id+"F4.boolean.opBoolean","INTERSECT",EDGE,{"derivedFrom":[subQ2,subQ3]})});}
            var Q1;
            {var subQ0=sQuery(id+"F7.wireOp",EDGE,"E8.0");var subQ1=sQuery(id+"F7.wireOp",EDGE,"E12");var subQ2=makeQuery(id+"F2.opExtrude","SWEPT_FACE",FACE,{"disambiguationData":[OSD([sQuery(id+"F1.wireOp",EDGE,"E1")])]});var subQ3=makeQuery(id+"F4.opExtrude","CAP_FACE",FACE,{"disambiguationData":[OSD([sQuery(id+"F3.wireOp",EDGE,"E2.bottom"),sQuery(id+"F3.wireOp",EDGE,"E2.top"),sQuery(id+"F3.wireOp",EDGE,"E2.left"),sQuery(id+"F3.wireOp",EDGE,"E2.right"),sQuery(id+"F3.wireOp",EDGE,"E3.filletArc"),sQuery(id+"F3.wireOp",EDGE,"E4.filletArc"),sQuery(id+"F3.wireOp",EDGE,"E5.filletArc"),sQuery(id+"F3.wireOp",EDGE,"E6.filletArc"),sQuery(id+"F3.wireOp",EDGE,"E7.0")])],"isStart":true});Q1=makeQuery(id+"F8.boolean.opBoolean","SPLIT",EDGE,{"disambiguationData":[TD([subQ2,subQ3,makeQuery(id+"F8.opExtrude","SWEPT_FACE",FACE,{"disambiguationData":[OSD([subQ0]),TDD([makeQuery(id+"F7.imprint","IMPRINT",EDGE,{"disambiguationData":[TD([[makeQuery(id+"F7.imprint","INTERSECT",VERTEX,{"derivedFrom":[subQ0,sQuery(id+"F7.wireOp",EDGE,"E13.MirrorCS"),sQuery(id+"F7.wireOp",EDGE,"E16")]}),-1.0]])],"derivedFrom":subQ0})])]}),makeQuery(id+"F8.opExtrude","SWEPT_FACE",FACE,{"disambiguationData":[OSD([subQ0]),TDD([makeQuery(id+"F7.imprint","IMPRINT",EDGE,{"disambiguationData":[TD([[makeQuery(id+"F7.imprint","INTERSECT",VERTEX,{"derivedFrom":[subQ0,sQuery(id+"F7.wireOp",EDGE,"E9"),sQuery(id+"F7.wireOp",EDGE,"E19")]}),-1.0]])],"derivedFrom":subQ0})])]}),makeQuery(id+"F8.opExtrude","SWEPT_FACE",FACE,{"disambiguationData":[OSD([subQ1])]})])],"derivedFrom":makeQuery(id+"F4.boolean.opBoolean","INTERSECT",EDGE,{"derivedFrom":[subQ2,subQ3]})});}
            var Q2;
            {var subQ0=sQuery(id+"F7.wireOp",EDGE,"E9");var subQ1=sQuery(id+"F7.wireOp",EDGE,"E8.0");var subQ2=sQuery(id+"F7.wireOp",EDGE,"E15.MirrorCS");var subQ3=makeQuery(id+"F2.opExtrude","SWEPT_FACE",FACE,{"disambiguationData":[OSD([sQuery(id+"F1.wireOp",EDGE,"E1")])]});var subQ4=makeQuery(id+"F4.opExtrude","CAP_FACE",FACE,{"disambiguationData":[OSD([sQuery(id+"F3.wireOp",EDGE,"E2.bottom"),sQuery(id+"F3.wireOp",EDGE,"E2.top"),sQuery(id+"F3.wireOp",EDGE,"E2.left"),sQuery(id+"F3.wireOp",EDGE,"E2.right"),sQuery(id+"F3.wireOp",EDGE,"E3.filletArc"),sQuery(id+"F3.wireOp",EDGE,"E4.filletArc"),sQuery(id+"F3.wireOp",EDGE,"E5.filletArc"),sQuery(id+"F3.wireOp",EDGE,"E6.filletArc"),sQuery(id+"F3.wireOp",EDGE,"E7.0")])],"isStart":true});Q2=makeQuery(id+"F8.boolean.opBoolean","SPLIT",EDGE,{"disambiguationData":[TD([subQ3,subQ4,makeQuery(id+"F8.opExtrude","SWEPT_FACE",FACE,{"disambiguationData":[OSD([subQ1]),TDD([makeQuery(id+"F7.imprint","IMPRINT",EDGE,{"disambiguationData":[TD([[makeQuery(id+"F7.imprint","INTERSECT",VERTEX,{"derivedFrom":[subQ1,sQuery(id+"F7.wireOp",EDGE,"E13.MirrorCS"),sQuery(id+"F7.wireOp",EDGE,"E16")]}),-1.0]])],"derivedFrom":subQ1})])]}),makeQuery(id+"F8.opExtrude","SWEPT_FACE",FACE,{"disambiguationData":[OSD([subQ1]),TDD([makeQuery(id+"F7.imprint","IMPRINT",EDGE,{"disambiguationData":[TD([[makeQuery(id+"F7.imprint","INTERSECT",VERTEX,{"derivedFrom":[subQ1,subQ0,sQuery(id+"F7.wireOp",EDGE,"E19")]}),-1.0]])],"derivedFrom":subQ1})])]}),makeQuery(id+"F8.opExtrude","SWEPT_FACE",FACE,{"disambiguationData":[OSD([subQ0])]}),makeQuery(id+"F8.opExtrude","SWEPT_FACE",FACE,{"disambiguationData":[OSD([subQ2])]})]),OD(1.0)],"derivedFrom":makeQuery(id+"F4.boolean.opBoolean","INTERSECT",EDGE,{"derivedFrom":[subQ3,subQ4]})});}
            var Q3;
            {var subQ0=sQuery(id+"F7.wireOp",EDGE,"E9");var subQ1=sQuery(id+"F7.wireOp",EDGE,"E8.0");var subQ2=sQuery(id+"F7.wireOp",EDGE,"E15.MirrorCS");var subQ3=makeQuery(id+"F2.opExtrude","SWEPT_FACE",FACE,{"disambiguationData":[OSD([sQuery(id+"F1.wireOp",EDGE,"E1")])]});var subQ4=makeQuery(id+"F4.opExtrude","CAP_FACE",FACE,{"disambiguationData":[OSD([sQuery(id+"F3.wireOp",EDGE,"E2.bottom"),sQuery(id+"F3.wireOp",EDGE,"E2.top"),sQuery(id+"F3.wireOp",EDGE,"E2.left"),sQuery(id+"F3.wireOp",EDGE,"E2.right"),sQuery(id+"F3.wireOp",EDGE,"E3.filletArc"),sQuery(id+"F3.wireOp",EDGE,"E4.filletArc"),sQuery(id+"F3.wireOp",EDGE,"E5.filletArc"),sQuery(id+"F3.wireOp",EDGE,"E6.filletArc"),sQuery(id+"F3.wireOp",EDGE,"E7.0")])],"isStart":true});Q3=makeQuery(id+"F8.boolean.opBoolean","SPLIT",EDGE,{"disambiguationData":[TD([subQ3,subQ4,makeQuery(id+"F8.opExtrude","SWEPT_FACE",FACE,{"disambiguationData":[OSD([subQ1]),TDD([makeQuery(id+"F7.imprint","IMPRINT",EDGE,{"disambiguationData":[TD([[makeQuery(id+"F7.imprint","INTERSECT",VERTEX,{"derivedFrom":[subQ1,sQuery(id+"F7.wireOp",EDGE,"E13.MirrorCS"),sQuery(id+"F7.wireOp",EDGE,"E16")]}),-1.0]])],"derivedFrom":subQ1})])]}),makeQuery(id+"F8.opExtrude","SWEPT_FACE",FACE,{"disambiguationData":[OSD([subQ1]),TDD([makeQuery(id+"F7.imprint","IMPRINT",EDGE,{"disambiguationData":[TD([[makeQuery(id+"F7.imprint","INTERSECT",VERTEX,{"derivedFrom":[subQ1,subQ0,sQuery(id+"F7.wireOp",EDGE,"E19")]}),-1.0]])],"derivedFrom":subQ1})])]}),makeQuery(id+"F8.opExtrude","SWEPT_FACE",FACE,{"disambiguationData":[OSD([subQ0])]}),makeQuery(id+"F8.opExtrude","SWEPT_FACE",FACE,{"disambiguationData":[OSD([subQ2])]})]),OD(0.0)],"derivedFrom":makeQuery(id+"F4.boolean.opBoolean","INTERSECT",EDGE,{"derivedFrom":[subQ3,subQ4]})});}
            fillet(context, id + "F19", {"entities" : qUnion([Q0, Q1, Q2, Q3]), "radius" : 3 * mm, "tangentPropagation" : true, "allowEdgeOverflow" : false});
        }
    });
